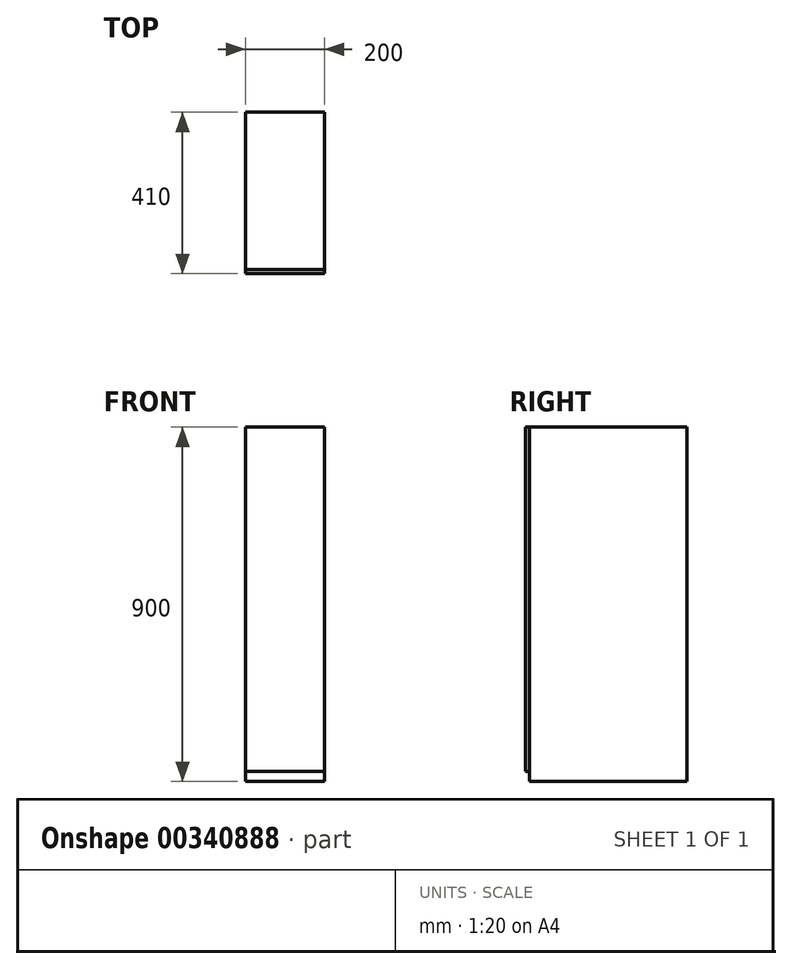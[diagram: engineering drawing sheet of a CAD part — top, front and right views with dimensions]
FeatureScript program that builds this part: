
annotation { "Feature Type Name" : "Feature", "Feature Type Description" : "" }
export const myFeature = defineFeature(function(context is Context, id is Id, definition is map)
    precondition{}
    {
        {
            var Q0;
            Q0=qCreatedBy(makeId("Top.planeOp"),FACE);
            var sketch = newSketch(context, id + "F0", { "sketchPlane" : qUnion([Q0])});
            skLineSegment(sketch, "E0.bottom", {"start": v(-150.3, 287.1) * mm, "end": v(49.7, 287.1) * mm});
            skLineSegment(sketch, "E0.top", {"start": v(-150.3, -112.9) * mm, "end": v(49.7, -112.9) * mm});
            skLineSegment(sketch, "E0.left", {"start": v(-150.3, 287.1) * mm, "end": v(-150.3, -112.9) * mm});
            skLineSegment(sketch, "E0.right", {"start": v(49.7, 287.1) * mm, "end": v(49.7, -112.9) * mm});
            skLineSegment(sketch, "E1.top", {"start": v(-150.3, -122.9) * mm, "end": v(49.7, -122.9) * mm});
            skLineSegment(sketch, "E1.left", {"start": v(-150.3, -112.9) * mm, "end": v(-150.3, -122.9) * mm});
            skLineSegment(sketch, "E1.right", {"start": v(49.7, -112.9) * mm, "end": v(49.7, -122.9) * mm});
            skSolve(sketch);
        }
        {
            var Q0;
            Q0=makeQuery(id+"F0.imprint","IMPRINT",FACE,{"disambiguationData":[TD([[makeQuery(id+"F0.imprint","IMPRINT",EDGE,{"derivedFrom":sQuery(id+"F0.wireOp",EDGE,"E0.bottom")}),-1.0]])]});
            extrude(context, id + "F1", {"entities" : qUnion([Q0]), "depth" : 900 * mm});
        }
        {
            var Q0;
            Q0=makeQuery(id+"F0.imprint","IMPRINT",FACE,{"disambiguationData":[TD([[makeQuery(id+"F0.imprint","IMPRINT",EDGE,{"derivedFrom":sQuery(id+"F0.wireOp",EDGE,"E1.top")}),1.0]])]});
            extrude(context, id + "F2", {"entities" : qUnion([Q0]), "depth" : 900 * mm, "hasSecondDirection" : true, "secondDirectionOppositeDirection" : false, "secondDirectionDepth" : 25 * mm});
        }
    });
